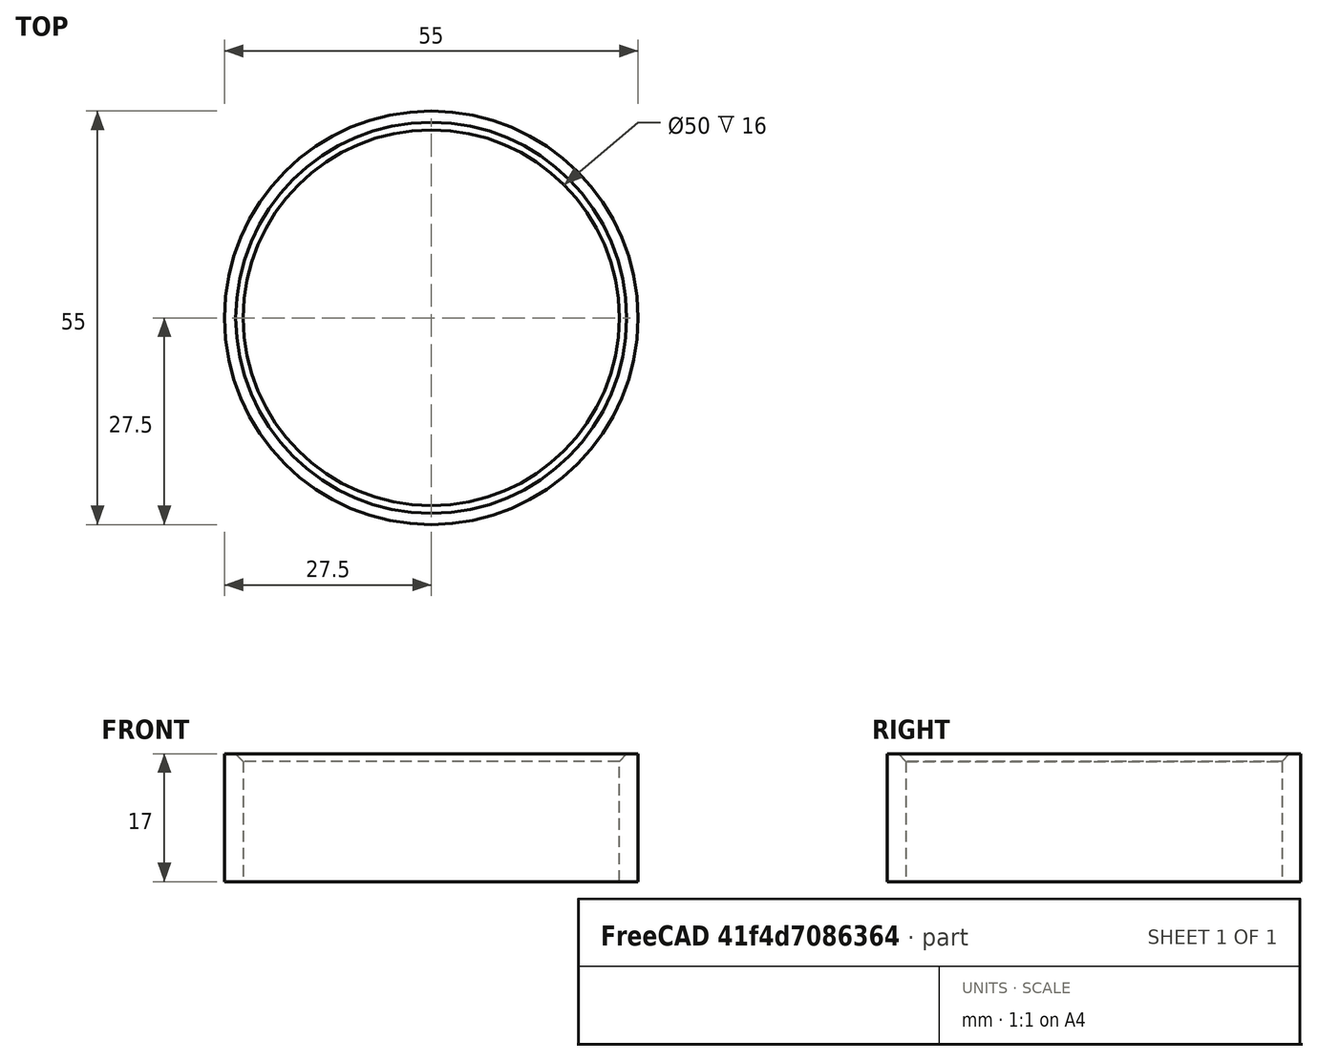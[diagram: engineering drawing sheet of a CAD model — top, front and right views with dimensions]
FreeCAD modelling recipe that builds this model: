
FCSTD DOCUMENT  (FreeCAD 0.19R24276 (Git))
Label: Stopper
License: All rights reserved
LicenseURL: http://en.wikipedia.org/wiki/All_rights_reserved
objects: Sketcher::SketchObject×1, PartDesign::Pad×1, PartDesign::Chamfer×1, PartDesign::Body×1
note: 6 computed .brp shape members not serialized (recipe doc carries the construction recipe); baked Part::Feature solids carry a one-line shape summary decoded from their .brp

FEATURE [Sketcher::SketchObject] Sketch
  FullyConstrained = true
  MapMode = 5
  Support = -> [XY_Plane]
  sketch-geometry (2):
    g0: Circle CenterX=0 CenterY=0 CenterZ=0 NormalX=0 NormalY=0 NormalZ=1 AngleXU=0 Radius=25
    g1: Circle CenterX=0 CenterY=0 CenterZ=0 NormalX=0 NormalY=0 NormalZ=1 AngleXU=0 Radius=27.5
  constraints (4):
    c: Coincident(g0,g-1)
    c: Coincident(g1,g0)
    c: Diameter(g0) = 50
    c: Diameter(g1) = 55
FEATURE [PartDesign::Pad] Pad
  Direction = (1,1,1)
  Length = 17
  Length2 = 100
  Profile = -> Sketch
  Type = 0
FEATURE [PartDesign::Chamfer] Chamfer
  Angle = 45
  Base = -> Pad [Edge6]
  BaseFeature = -> Pad
  ChamferType = 0
  FlipDirection = false
  Size = 1
  Size2 = 1
  SupportTransform = false
FEATURE [PartDesign::Body] Body
  Group = -> [Sketch,Pad,Chamfer]
  Origin = -> Origin
  Tip = -> Chamfer
